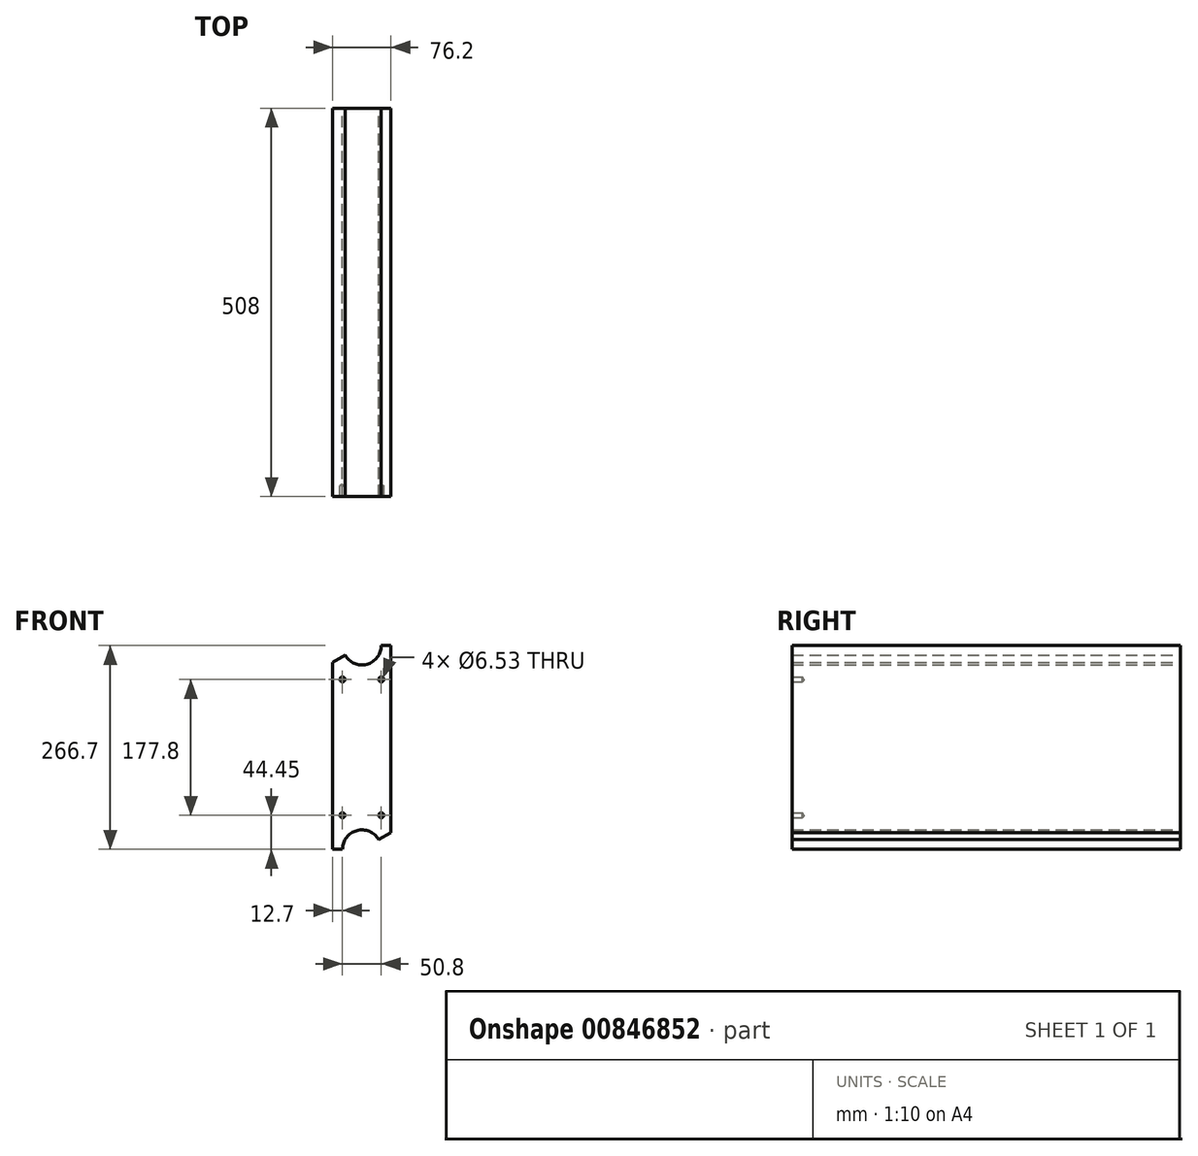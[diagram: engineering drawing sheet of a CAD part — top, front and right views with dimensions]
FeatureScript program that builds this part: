
annotation { "Feature Type Name" : "Feature", "Feature Type Description" : "" }
export const myFeature = defineFeature(function(context is Context, id is Id, definition is map)
    precondition{}
    {
        {
            var Q0;
            Q0=qCreatedBy(makeId("Front.planeOp"),FACE);
            var sketch = newSketch(context, id + "F0", { "sketchPlane" : qUnion([Q0])});
            skLineSegment(sketch, "E0.top", {"start": v(-38.1, -133.35) * mm, "end": v(-25.4, -133.35) * mm});
            skLineSegment(sketch, "E0.left", {"start": v(-38.1, 111.35) * mm, "end": v(-38.1, -133.35) * mm});
            skLineSegment(sketch, "E0.right", {"start": v(38.1, 133.35) * mm, "end": v(38.1, -111.35) * mm});
            skLineSegment(sketch, "E1", {"start": v(-38.1, -133.35) * mm, "end": v(38.1, 133.35) * mm});
            skArc(sketch, "E2", {"start": v(-22, 120.65) * mm, "mid": v(6.57, 108.82) * mm, "end": v(25.4, 133.35) * mm});
            skArc(sketch, "E3", {"start": v(22, -120.65) * mm, "mid": v(-6.57, -108.82) * mm, "end": v(-25.4, -133.35) * mm});
            skLineSegment(sketch, "E4.trimOffspring", {"start": v(25.4, 133.35) * mm, "end": v(38.1, 133.35) * mm});
            skLineSegment(sketch, "E5", {"start": v(22, -120.65) * mm, "end": v(38.1, -111.35) * mm});
            skLineSegment(sketch, "E6", {"start": v(-22, 120.65) * mm, "end": v(-38.1, 111.35) * mm});
            skPoint(sketch, "E0.bottom.start.orphan", {"position": v(-38.1, 133.35) * mm});
            skPoint(sketch, "E7.trimOffspring.end.orphan", {"position": v(38.1, -133.35) * mm});
            skLineSegment(sketch, "E8", {"start": v(0, 133.35) * mm, "end": v(0, -133.35) * mm, "construction": true});
            skSolve(sketch);
        }
        {
            var Q0;
            Q0=makeQuery(id+"F0.imprint","IMPRINT",FACE,{"disambiguationData":[TD([[makeQuery(id+"F0.imprint","IMPRINT",EDGE,{"derivedFrom":sQuery(id+"F0.wireOp",EDGE,"E0.left")}),1.0]])]});
            var Q1;
            Q1=makeQuery(id+"F0.imprint","IMPRINT",FACE,{"disambiguationData":[TD([[makeQuery(id+"F0.imprint","IMPRINT",EDGE,{"derivedFrom":sQuery(id+"F0.wireOp",EDGE,"E0.top")}),1.0]])]});
            extrude(context, id + "F1", {"entities" : qUnion([Q0, Q1]), "depth" : 508 * mm, "offsetDistance" : 25.4 * mm, "symmetric" : true});
        }
        {
            var Q0;
            Q0=makeQuery(id+"F1.opExtrude","CAP_FACE",FACE,{"disambiguationData":[OSD([sQuery(id+"F0.wireOp",EDGE,"E0.top"),sQuery(id+"F0.wireOp",EDGE,"E0.left"),sQuery(id+"F0.wireOp",EDGE,"E0.right"),sQuery(id+"F0.wireOp",EDGE,"E2"),sQuery(id+"F0.wireOp",EDGE,"E3"),sQuery(id+"F0.wireOp",EDGE,"E4.trimOffspring"),sQuery(id+"F0.wireOp",EDGE,"E5"),sQuery(id+"F0.wireOp",EDGE,"E6")])],"isStart":false});
            var sketch = newSketch(context, id + "F2", { "sketchPlane" : qUnion([Q0])});
            skLineSegment(sketch, "E9", {"start": v(0, 88.9) * mm, "end": v(0, -88.9) * mm});
            skLineSegment(sketch, "E10", {"start": v(-25.4, 88.9) * mm, "end": v(25.4, 88.9) * mm});
            skLineSegment(sketch, "E11", {"start": v(-25.4, -88.9) * mm, "end": v(25.4, -88.9) * mm});
            skPoint(sketch, "E12", {"position": v(0, 133.35) * mm});
            skPoint(sketch, "E13", {"position": v(-25.4, 88.9) * mm});
            skPoint(sketch, "E14", {"position": v(25.4, 88.9) * mm});
            skPoint(sketch, "E15", {"position": v(-25.4, -88.9) * mm});
            skPoint(sketch, "E16", {"position": v(25.4, -88.9) * mm});
            skSolve(sketch);
        }
        {
            var Q0;
            Q0=sQuery(id+"F2.wireOp",VERTEX,"E13");
            var Q1;
            Q1=sQuery(id+"F2.wireOp",VERTEX,"E14");
            var Q2;
            Q2=sQuery(id+"F2.wireOp",VERTEX,"E15");
            var Q3;
            Q3=sQuery(id+"F2.wireOp",VERTEX,"E16");
            var Q4;
            Q4=makeQuery(id+"F1.opExtrude","SWEPT_BODY",BODY,{"disambiguationData":[OSD([sQuery(id+"F0.wireOp",EDGE,"E0.top"),sQuery(id+"F0.wireOp",EDGE,"E0.left"),sQuery(id+"F0.wireOp",EDGE,"E0.right"),sQuery(id+"F0.wireOp",EDGE,"E2"),sQuery(id+"F0.wireOp",EDGE,"E3"),sQuery(id+"F0.wireOp",EDGE,"E4.trimOffspring"),sQuery(id+"F0.wireOp",EDGE,"E5"),sQuery(id+"F0.wireOp",EDGE,"E6")])]});
            hole(context, id + "F3", {"style" : HoleStyle.SIMPLE, "endStyle" : HoleEndStyle.BLIND, "standardTappedOrClearance" : lookupTablePath({ "standard" : "ANSI", "engagement" : "75%", "pitch" : "18 tpi", "size" : "5/16", "type" : "Tapped" }), "standardBlindInLast" : lookupTablePath({ "standard" : "ANSI", "fit" : "Free", "engagement" : "75%", "pitch" : "18 tpi", "size" : "5/16", "type" : "Clearance & tapped" }), "holeDiameter" : 6.53 * mm, "majorDiameter" : 7.94 * mm, "showTappedDepth" : true, "holeDepth" : 13.76 * mm, "tappedDepth" : 9.52 * mm, "tapClearance" : 3, "locations" : qUnion([Q0, Q1, Q2, Q3]), "scope" : qUnion([Q4]), "startStyle" : HoleStartStyle.SKETCH});
        }
    });
